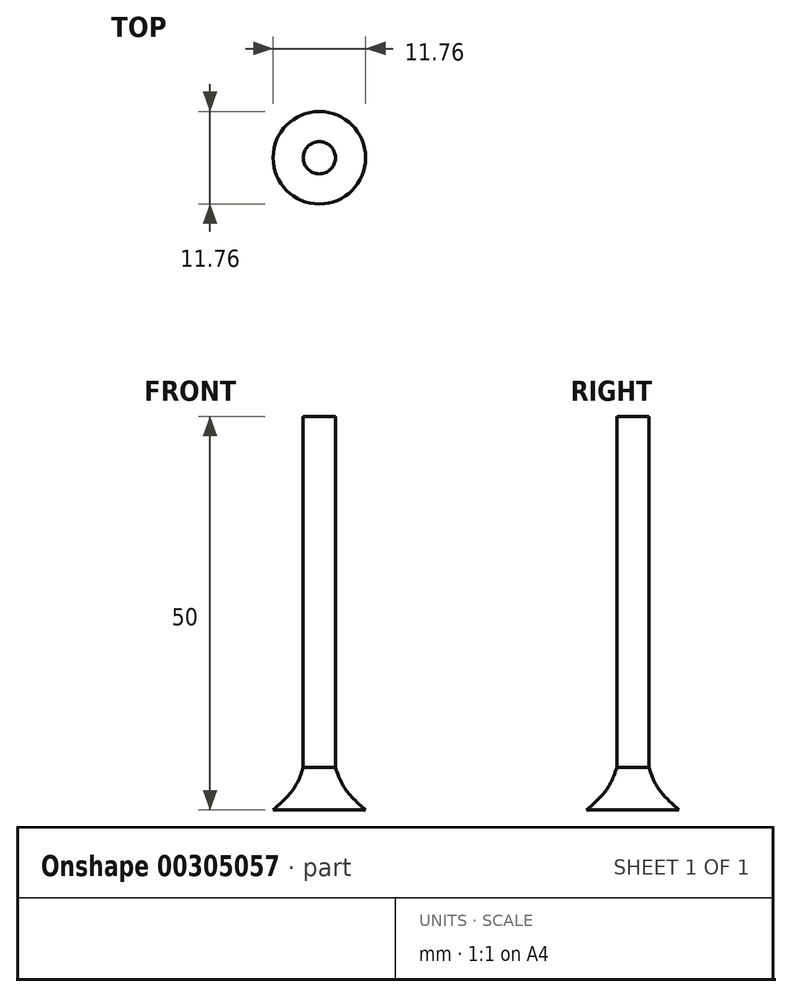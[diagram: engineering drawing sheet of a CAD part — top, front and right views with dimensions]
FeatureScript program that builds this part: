
annotation { "Feature Type Name" : "Feature", "Feature Type Description" : "" }
export const myFeature = defineFeature(function(context is Context, id is Id, definition is map)
    precondition{}
    {
        {
            var Q0;
            Q0=qCreatedBy(makeId("Top.planeOp"),FACE);
            var sketch = newSketch(context, id + "F0", { "sketchPlane" : qUnion([Q0])});
            skCircle(sketch, "E0", {"center": v(0, 0) * mm, "radius": 5.88 * mm});
            skSolve(sketch);
        }
        {
            var Q0;
            Q0=qCreatedBy(makeId("Top.planeOp"),FACE);
            cPlane(context, id + "F1", {"entities" : qUnion([Q0]), "cplaneType" : CPlaneType.OFFSET, "offset" : 3.4 * mm, "width" : 150 * mm, "height" : 150 * mm});
        }
        {
            var Q0;
            Q0=qCreatedBy(id+"F1.planeOp",FACE);
            var sketch = newSketch(context, id + "F2", { "sketchPlane" : qUnion([Q0])});
            skCircle(sketch, "E1", {"center": v(0, 0) * mm, "radius": 2.85 * mm});
            skSolve(sketch);
        }
        {
            var Q0;
            Q0=qCreatedBy(makeId("Top.planeOp"),FACE);
            cPlane(context, id + "F3", {"entities" : qUnion([Q0]), "cplaneType" : CPlaneType.OFFSET, "offset" : 5.4 * mm, "width" : 150 * mm, "height" : 150 * mm});
        }
        {
            var Q0;
            Q0=qCreatedBy(id+"F3.planeOp",FACE);
            var sketch = newSketch(context, id + "F4", { "sketchPlane" : qUnion([Q0])});
            skCircle(sketch, "E2", {"center": v(0, 0) * mm, "radius": 2.05 * mm});
            skSolve(sketch);
        }
        {
            var Q0;
            Q0=qCreatedBy(makeId("Top.planeOp"),FACE);
            cPlane(context, id + "F5", {"entities" : qUnion([Q0]), "cplaneType" : CPlaneType.OFFSET, "offset" : 50 * mm, "width" : 150 * mm, "height" : 150 * mm});
        }
        {
            var Q0;
            Q0=qCreatedBy(id+"F5.planeOp",FACE);
            var sketch = newSketch(context, id + "F6", { "sketchPlane" : qUnion([Q0])});
            skCircle(sketch, "E3", {"center": v(0, 0) * mm, "radius": 2.05 * mm});
            skSolve(sketch);
        }
        {
            var Q0;
            Q0=makeQuery(id+"F0.imprint","IMPRINT",FACE,{"disambiguationData":[TD([[makeQuery(id+"F0.imprint","IMPRINT",EDGE,{"derivedFrom":sQuery(id+"F0.wireOp",EDGE,"E0")}),1.0]])]});
            var Q1;
            Q1=makeQuery(id+"F2.imprint","IMPRINT",FACE,{"disambiguationData":[TD([[makeQuery(id+"F2.imprint","IMPRINT",EDGE,{"derivedFrom":sQuery(id+"F2.wireOp",EDGE,"E1")}),1.0]])]});
            var Q2;
            Q2=makeQuery(id+"F4.imprint","IMPRINT",FACE,{"disambiguationData":[TD([[makeQuery(id+"F4.imprint","IMPRINT",EDGE,{"derivedFrom":sQuery(id+"F4.wireOp",EDGE,"E2")}),1.0]])]});
            loft(context, id + "F7", {"sheetProfilesArray" : [{ "sheetProfileEntities" : qUnion([Q0]) }, { "sheetProfileEntities" : qUnion([Q1]) }, { "sheetProfileEntities" : qUnion([Q2]) }]});
        }
        {
            var Q0;
            Q0=makeQuery(id+"F7.opLoft","CAP_FACE",FACE,{"disambiguationData":[OSD([makeQuery(id+"F4.imprint","IMPRINT",FACE,{"disambiguationData":[TD([[makeQuery(id+"F4.imprint","IMPRINT",EDGE,{"derivedFrom":sQuery(id+"F4.wireOp",EDGE,"E2")}),1.0]])]})])],"isStart":true});
            var Q1;
            Q1=sQuery(id+"F6.wireOp",VERTEX,"E3.center");
            extrude(context, id + "F8", {"entities" : qUnion([Q0]), "operationType" : NewBodyOperationType.ADD, "endBound" : BoundingType.UP_TO_VERTEX, "endBoundEntityVertex" : qUnion([Q1]), "depth" : 25 * mm});
        }
    });
